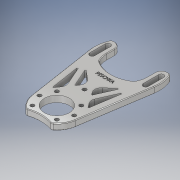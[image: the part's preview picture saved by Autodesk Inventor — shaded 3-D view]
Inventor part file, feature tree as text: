
AUTODESK INVENTOR PART (.ipt)
format: ipt  version: 2019.3 (Build 233278000, 278)  size: 674,816 bytes
history: native  units: mm
features: thread x7, emboss x2, fillet x2, sketch x2, extrude x1, chamfer x1, other x1
ambient origin geometry x8: Origin, YZ Plane, XZ Plane, XY Plane, X Axis, Y Axis, Z Axis, Center Point
bodies: Body1 (feature_tree)
feature tree (16):
  extrude  "Extrusion3"  Depth=20.0mm
  thread  "Thread1"  [1 undecoded]
  thread  "Thread2"  [1 undecoded]
  thread  "Thread3"  [1 undecoded]
  thread  "Thread4"  [1 undecoded]
  thread  "Thread5"  [1 undecoded]
  thread  "Thread6"  [1 undecoded]
  thread  "Thread7"  [1 undecoded]
  emboss  "Emboss1"
  emboss  "Emboss2"
  fillet  "Fillet3"  Radius=3.0mm
  fillet  "Fillet5"  Radius=3.0mm
  chamfer  "Chamfer3"  Distance=3.0mm
  other  "Center Lines"
  sketch  "Sketch1"  dims[d0=55.6mm d1=20.0mm d3=3.5mm d4=3.5mm d5=7.0mm d7=43.0mm d9=3.5mm d11=32.0mm d15=4.0mm d24=3.0mm d25=3.0mm]
  sketch  "Sketch3"  dims[d27=45.0deg d29=3.0mm d30=3.0mm d31=22.0mm d40=5.0mm d41=0.0mm d44=10.0mm d45=0.0mm d46=10.0mm d47=0.0mm d48=10.0mm d49=0.0mm d50=20.0mm d51=52.0mm d53=26.0mm d54=10.0mm d55=0.0mm d56=10.0mm d57=0.0mm d58=10.0mm d59=0.0mm d60=10.0mm d61=0.0mm d65=0.2mm d66=0.0mm d67=14.0mm d68=14.0mm d69=5.0mm d70=15.0mm d71=5.0mm d72=15.0mm d73=0.2mm d74=0.0mm d75=84.563203mm d76=7.5mm d77=3.75mm d78=1.0mm d81=6.25mm d82=12.5mm d85=5.0mm d86=4.0mm d91=0.5mm d94=2.0mm d95=0.5mm d96=2.0mm d97=45.0deg d98=15.0deg d99=24.0mm]
note: 7 required parameter values undecoded (feature->parameter linkage not recoverable at this tier; creation-order binding heuristic only, values carry confidence <= 0.55)
